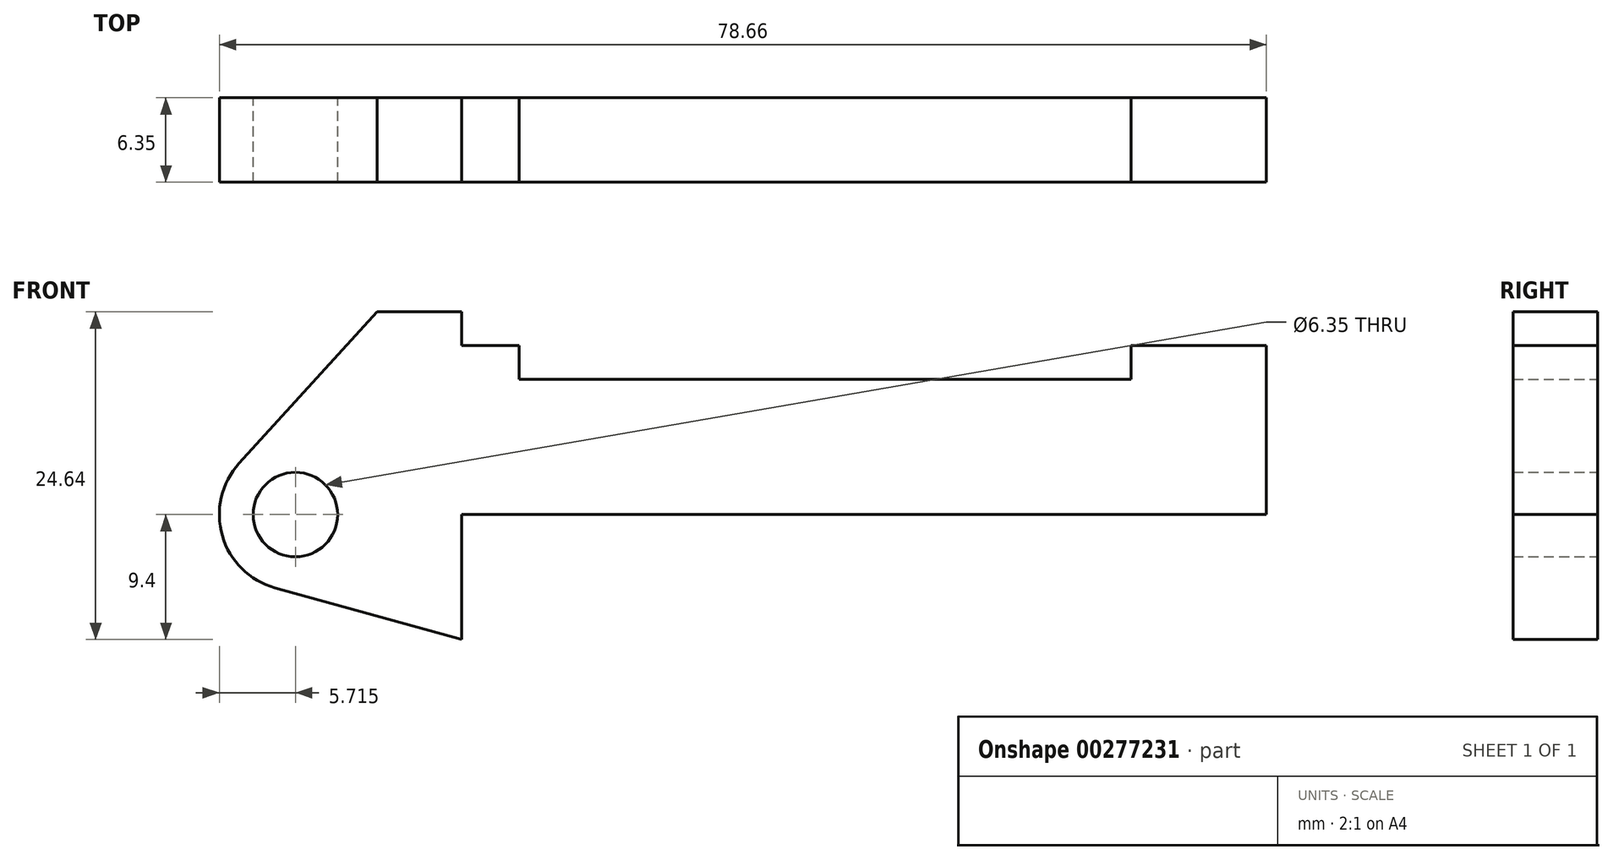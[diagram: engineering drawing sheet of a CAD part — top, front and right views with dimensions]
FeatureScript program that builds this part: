
annotation { "Feature Type Name" : "Feature", "Feature Type Description" : "" }
export const myFeature = defineFeature(function(context is Context, id is Id, definition is map)
    precondition{}
    {
        {
            var Q0;
            Q0=qCreatedBy(makeId("Front.planeOp"),FACE);
            var sketch = newSketch(context, id + "F0", { "sketchPlane" : qUnion([Q0])});
            skLineSegment(sketch, "E0", {"start": v(0, 0) * mm, "end": v(0, 12.7) * mm});
            skLineSegment(sketch, "E1", {"start": v(0, 12.7) * mm, "end": v(10.16, 12.7) * mm});
            skLineSegment(sketch, "E2", {"start": v(10.16, 12.7) * mm, "end": v(10.16, 10.16) * mm});
            skLineSegment(sketch, "E3", {"start": v(10.16, 10.16) * mm, "end": v(56.13, 10.16) * mm});
            skLineSegment(sketch, "E4", {"start": v(56.13, 10.16) * mm, "end": v(56.13, 12.7) * mm});
            skLineSegment(sketch, "E5", {"start": v(56.13, 12.7) * mm, "end": v(66.3, 12.7) * mm});
            skLineSegment(sketch, "E6", {"start": v(66.3, 12.7) * mm, "end": v(66.3, 0) * mm});
            skLineSegment(sketch, "E7", {"start": v(66.3, 0) * mm, "end": v(0, 0) * mm});
            skLineSegment(sketch, "E8", {"start": v(5.84, 15.24) * mm, "end": v(-0.5, 15.24) * mm});
            skLineSegment(sketch, "E9", {"start": v(-0.5, 15.24) * mm, "end": v(-10.88, 3.85) * mm});
            skLineSegment(sketch, "E10", {"start": v(0, 0) * mm, "end": v(-6.65, 0) * mm});
            skCircle(sketch, "E11", {"center": v(-6.65, 0) * mm, "radius": 5.72 * mm});
            skCircle(sketch, "E12", {"center": v(-6.65, 0) * mm, "radius": 3.18 * mm});
            skLineSegment(sketch, "E13", {"start": v(5.84, 15.24) * mm, "end": v(5.84, -9.4) * mm});
            skLineSegment(sketch, "E14", {"start": v(5.84, -9.4) * mm, "end": v(-8.18, -5.5) * mm});
            skSolve(sketch);
        }
        {
            var Q0;
            {var subQ0=sQuery(id+"F0.wireOp",EDGE,"E14");Q0=makeQuery(id+"F0.imprint","IMPRINT",FACE,{"disambiguationData":[TD([[makeQuery(id+"F0.imprint","IMPRINT",EDGE,{"derivedFrom":subQ0}),-1.0]])]});}
            var Q1;
            {var subQ4=sQuery(id+"F0.wireOp",EDGE,"E12");Q1=makeQuery(id+"F0.imprint","IMPRINT",FACE,{"disambiguationData":[TD([[makeQuery(id+"F0.imprint","IMPRINT",EDGE,{"derivedFrom":subQ4}),-1.0]])]});}
            var Q2;
            {var subQ3=sQuery(id+"F0.wireOp",EDGE,"E0");Q2=makeQuery(id+"F0.imprint","IMPRINT",FACE,{"disambiguationData":[TD([[makeQuery(id+"F0.imprint","IMPRINT",EDGE,{"derivedFrom":subQ3}),1.0]])]});}
            var Q3;
            {var subQ0=sQuery(id+"F0.wireOp",EDGE,"E0");Q3=makeQuery(id+"F0.imprint","IMPRINT",FACE,{"disambiguationData":[TD([[makeQuery(id+"F0.imprint","IMPRINT",EDGE,{"derivedFrom":subQ0}),-1.0]])]});}
            var Q4;
            {var subQ0=sQuery(id+"F0.wireOp",EDGE,"E2");Q4=makeQuery(id+"F0.imprint","IMPRINT",FACE,{"disambiguationData":[TD([[makeQuery(id+"F0.imprint","IMPRINT",EDGE,{"derivedFrom":subQ0}),-1.0]])]});}
            extrude(context, id + "F1", {"entities" : qUnion([Q0, Q1, Q2, Q3, Q4]), "depth" : 6.35 * mm});
        }
    });
